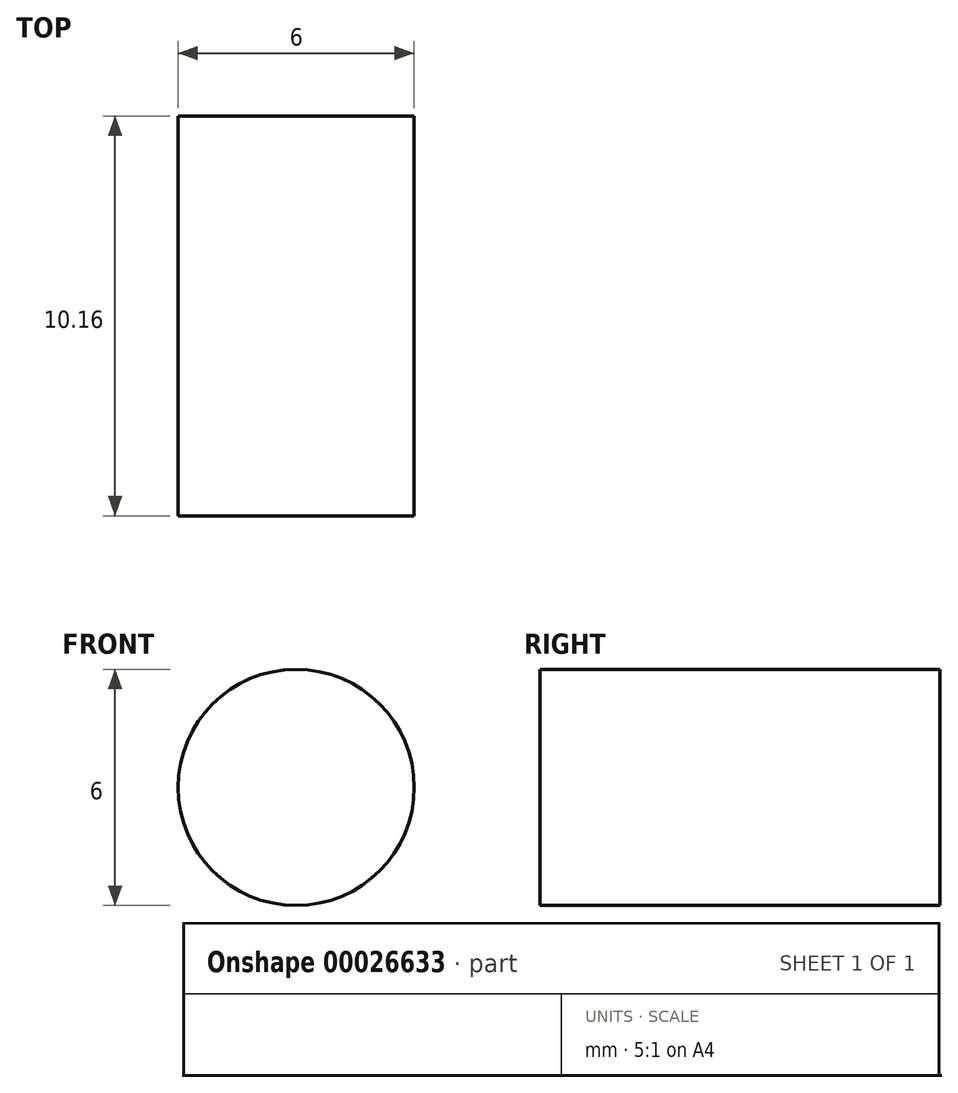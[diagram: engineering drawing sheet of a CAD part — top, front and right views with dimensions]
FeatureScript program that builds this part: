
annotation { "Feature Type Name" : "Feature", "Feature Type Description" : "" }
export const myFeature = defineFeature(function(context is Context, id is Id, definition is map)
    precondition{}
    {
        {
            var Q0;
            Q0=qCreatedBy(makeId("Front.planeOp"),FACE);
            var sketch = newSketch(context, id + "F0", { "sketchPlane" : qUnion([Q0])});
            skCircle(sketch, "E0", {"center": v(0, 0) * mm, "radius": 3 * mm});
            skSolve(sketch);
        }
        {
            var Q0;
            Q0=makeQuery(id+"F0.imprint","IMPRINT",FACE,{"disambiguationData":[TD([[makeQuery(id+"F0.imprint","IMPRINT",EDGE,{"derivedFrom":sQuery(id+"F0.wireOp",EDGE,"E0")}),1.0]])]});
            extrude(context, id + "F1", {"entities" : qUnion([Q0]), "depth" : 10.16 * mm});
        }
    });
